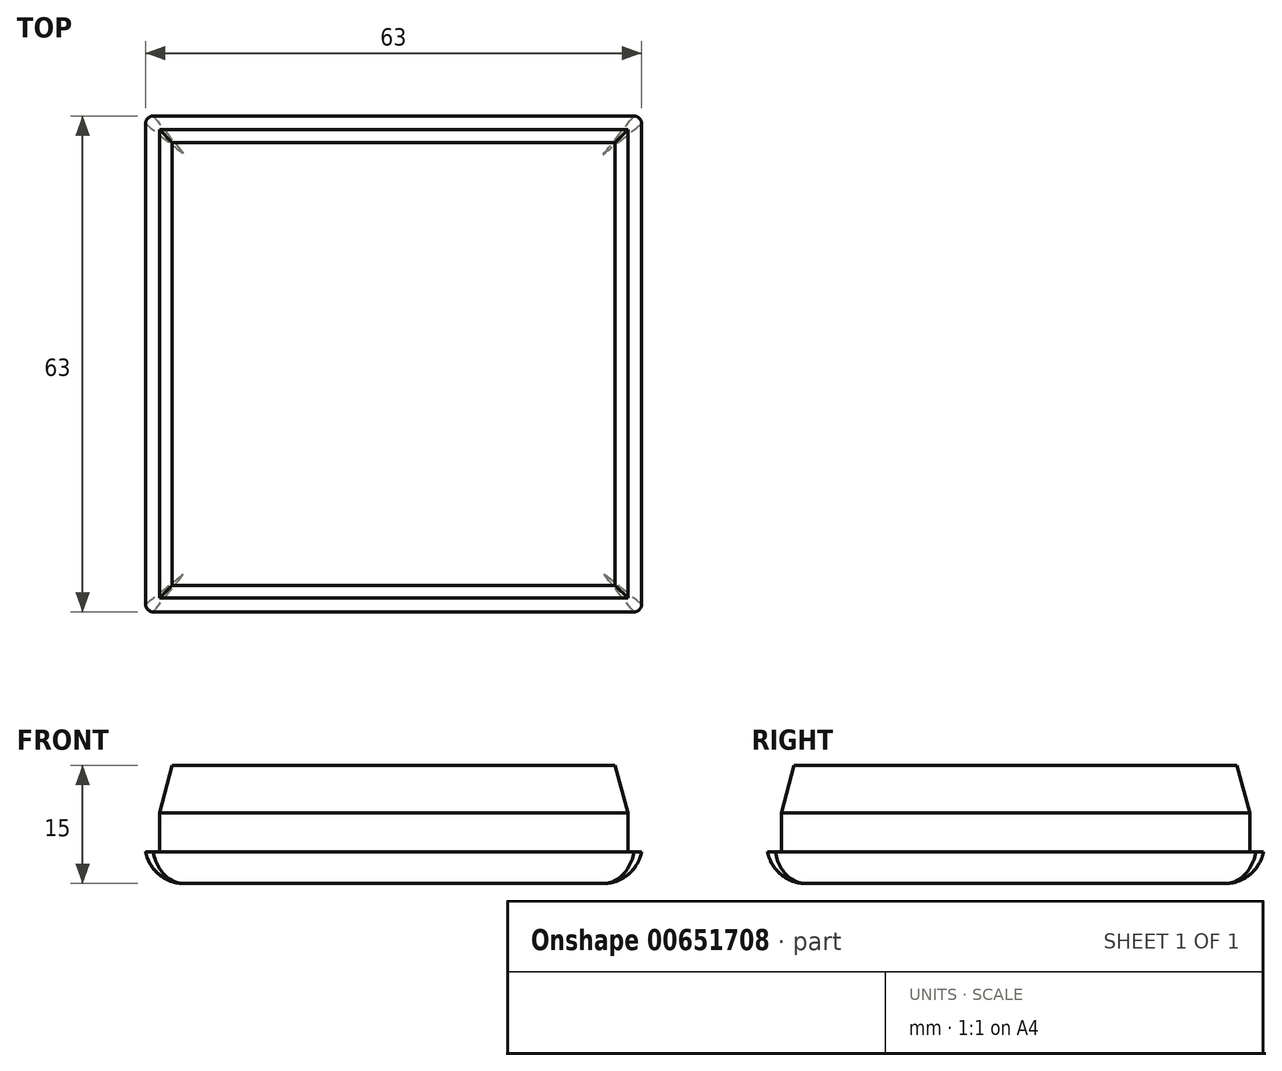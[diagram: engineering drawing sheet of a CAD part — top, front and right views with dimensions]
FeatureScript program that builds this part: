
annotation { "Feature Type Name" : "Feature", "Feature Type Description" : "" }
export const myFeature = defineFeature(function(context is Context, id is Id, definition is map)
    precondition{}
    {
        {
            var Q0;
            Q0=qCreatedBy(makeId("Top.planeOp"),FACE);
            var sketch = newSketch(context, id + "F0", { "sketchPlane" : qUnion([Q0])});
            skLineSegment(sketch, "E0.bottom", {"start": v(31.5, -31.5) * mm, "end": v(-31.5, -31.5) * mm});
            skLineSegment(sketch, "E0.top", {"start": v(31.5, 31.5) * mm, "end": v(-31.5, 31.5) * mm});
            skLineSegment(sketch, "E0.left", {"start": v(31.5, -31.5) * mm, "end": v(31.5, 31.5) * mm});
            skLineSegment(sketch, "E0.right", {"start": v(-31.5, -31.5) * mm, "end": v(-31.5, 31.5) * mm});
            skPoint(sketch, "E0.middle", {"position": v(0, 0) * mm});
            skLineSegment(sketch, "E1.bottom", {"start": v(29.75, -29.75) * mm, "end": v(-29.75, -29.75) * mm});
            skLineSegment(sketch, "E1.top", {"start": v(29.75, 29.75) * mm, "end": v(-29.75, 29.75) * mm});
            skLineSegment(sketch, "E1.left", {"start": v(29.75, -29.75) * mm, "end": v(29.75, 29.75) * mm});
            skLineSegment(sketch, "E1.right", {"start": v(-29.75, -29.75) * mm, "end": v(-29.75, 29.75) * mm});
            skSolve(sketch);
        }
        {
            var Q0;
            Q0=makeQuery(id+"F0.imprint","IMPRINT",FACE,{"disambiguationData":[TD([[makeQuery(id+"F0.imprint","IMPRINT",EDGE,{"derivedFrom":sQuery(id+"F0.wireOp",EDGE,"E1.bottom")}),-1.0]])]});
            extrude(context, id + "F1", {"entities" : qUnion([Q0]), "depth" : 15 * mm, "offsetDistance" : 25 * mm});
        }
        {
            var Q0;
            Q0=makeQuery(id+"F0.imprint","IMPRINT",FACE,{"disambiguationData":[TD([[makeQuery(id+"F0.imprint","IMPRINT",EDGE,{"derivedFrom":sQuery(id+"F0.wireOp",EDGE,"E0.bottom")}),-1.0]])]});
            extrude(context, id + "F2", {"entities" : qUnion([Q0]), "operationType" : NewBodyOperationType.ADD, "depth" : 4 * mm, "offsetDistance" : 25 * mm});
        }
        {
            var Q0;
            {var subQ0=sQuery(id+"F0.wireOp",EDGE,"E1.right");var subQ1=sQuery(id+"F0.wireOp",EDGE,"E1.left");var subQ2=sQuery(id+"F0.wireOp",EDGE,"E1.top");var subQ3=sQuery(id+"F0.wireOp",EDGE,"E1.bottom");Q0=makeQuery(id+"F2.boolean.opBoolean","MERGE",FACE,{"derivedFrom":[makeQuery(id+"F1.opExtrude","CAP_FACE",FACE,{"disambiguationData":[OSD([subQ3,subQ2,subQ1,subQ0])],"isStart":true}),makeQuery(id+"F2.opExtrude","CAP_FACE",FACE,{"disambiguationData":[OSD([sQuery(id+"F0.wireOp",EDGE,"E0.bottom"),sQuery(id+"F0.wireOp",EDGE,"E0.top"),sQuery(id+"F0.wireOp",EDGE,"E0.left"),sQuery(id+"F0.wireOp",EDGE,"E0.right"),subQ3,subQ2,subQ1,subQ0])],"isStart":true})]});}
            fillet(context, id + "F3", {"entities" : qUnion([Q0]), "radius" : 5 * mm, "tangentPropagation" : true, "allowEdgeOverflow" : false});
        }
        {
            var Q0;
            Q0=makeQuery(id+"F1.opExtrude","CAP_FACE",FACE,{"disambiguationData":[OSD([sQuery(id+"F0.wireOp",EDGE,"E1.bottom"),sQuery(id+"F0.wireOp",EDGE,"E1.top"),sQuery(id+"F0.wireOp",EDGE,"E1.left"),sQuery(id+"F0.wireOp",EDGE,"E1.right")])],"isStart":false});
            chamfer(context, id + "F4", {"entities" : qUnion([Q0]), "chamferType" : ChamferType.OFFSET_ANGLE, "width" : 6 * mm, "oppositeDirection" : false, "angle" : 15 * degree, "tangentPropagation" : true});
        }
        {
            var Q0;
            Q0=makeQuery(id+"F3.opFillet","BLEND_EDGE",EDGE,{"blendedFrom":[makeQuery(id+"F2.opExtrude","CAP_EDGE",EDGE,{"disambiguationData":[OSD([sQuery(id+"F0.wireOp",EDGE,"E0.bottom")])],"isStart":true}),makeQuery(id+"F2.opExtrude","CAP_EDGE",EDGE,{"disambiguationData":[OSD([sQuery(id+"F0.wireOp",EDGE,"E0.right")])],"isStart":true})],"blendedInto":[]});
            var Q1;
            Q1=makeQuery(id+"F3.opFillet","BLEND_EDGE",EDGE,{"blendedFrom":[makeQuery(id+"F2.opExtrude","CAP_EDGE",EDGE,{"disambiguationData":[OSD([sQuery(id+"F0.wireOp",EDGE,"E0.top")])],"isStart":true}),makeQuery(id+"F2.opExtrude","CAP_EDGE",EDGE,{"disambiguationData":[OSD([sQuery(id+"F0.wireOp",EDGE,"E0.right")])],"isStart":true})],"blendedInto":[]});
            var Q2;
            Q2=makeQuery(id+"F3.opFillet","BLEND_EDGE",EDGE,{"blendedFrom":[makeQuery(id+"F2.opExtrude","CAP_EDGE",EDGE,{"disambiguationData":[OSD([sQuery(id+"F0.wireOp",EDGE,"E0.top")])],"isStart":true}),makeQuery(id+"F2.opExtrude","CAP_EDGE",EDGE,{"disambiguationData":[OSD([sQuery(id+"F0.wireOp",EDGE,"E0.left")])],"isStart":true})],"blendedInto":[]});
            var Q3;
            Q3=makeQuery(id+"F3.opFillet","BLEND_EDGE",EDGE,{"blendedFrom":[makeQuery(id+"F2.opExtrude","CAP_EDGE",EDGE,{"disambiguationData":[OSD([sQuery(id+"F0.wireOp",EDGE,"E0.bottom")])],"isStart":true}),makeQuery(id+"F2.opExtrude","CAP_EDGE",EDGE,{"disambiguationData":[OSD([sQuery(id+"F0.wireOp",EDGE,"E0.left")])],"isStart":true})],"blendedInto":[]});
            fillet(context, id + "F5", {"entities" : qUnion([Q0, Q1, Q2, Q3]), "radius" : 1 * mm, "tangentPropagation" : true, "allowEdgeOverflow" : false});
        }
    });
